# Revit family: Loxos-Orthocreche_ouvert-3D-T-FBLR
name_source: partatom
category: Generic Models
units: mm (PartAtom-declared; Revit-internal decimal feet)

## family parameters
Always vertical = Yes
Can host rebar = No
Cut with Voids When Loaded = No
Part Type = Normal
Room Calculation Point = No
Round Connector Dimension = Use Diameter
Shared = No
Work Plane-Based = No

## types (1)
- Loxos-Orthocreche_ouvert-3D-T-FBLR
    Default Elevation = 0 mm  [stored 0 ft]
    Description = PETITE ENFANCE - LOXOS BAIN
    Fax = +33 (0)2 31 32 18 19
    Manufacturer = Loxos
    Model = Ortocreche ouvert
    Type Comments = Ces meubles répondent aux recommandations d’équipement sanitaire de la petite enfance
    Télephone = +33 (0)2 31 32 18 18
    URL = http://www.loxos.com

note: [stored X ft] marks values corroborated as IEEE doubles in the binary element streams (Revit-internal decimal feet)

## geometry (parser evidence)
native form markers: Sweep x3
no freeform markers — native parametric forms only
